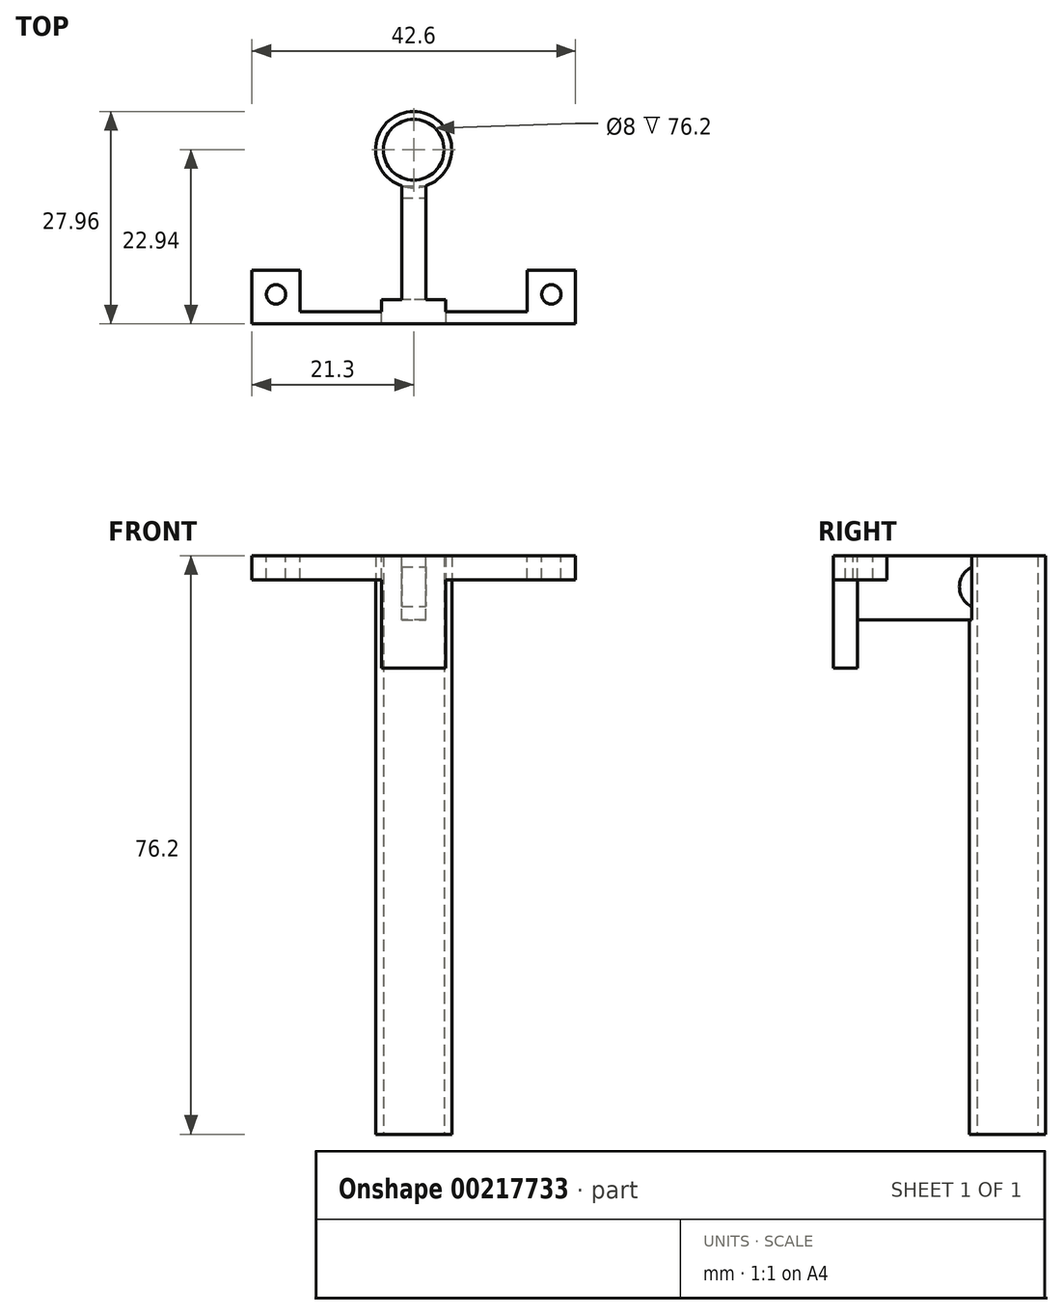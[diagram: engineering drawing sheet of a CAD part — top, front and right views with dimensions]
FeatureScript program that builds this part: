
annotation { "Feature Type Name" : "Feature", "Feature Type Description" : "" }
export const myFeature = defineFeature(function(context is Context, id is Id, definition is map)
    precondition{}
    {
        {
            var Q0;
            Q0=qCreatedBy(makeId("Top.planeOp"),FACE);
            var sketch = newSketch(context, id + "F0", { "sketchPlane" : qUnion([Q0])});
            skCircle(sketch, "E0", {"center": v(0, 0) * mm, "radius": 4 * mm});
            skCircle(sketch, "E1", {"center": v(0, 0) * mm, "radius": 5.02 * mm});
            skSolve(sketch);
        }
        {
            var Q0;
            Q0 = qSketchRegion(id + "F0", true);
            extrude(context, id + "F1", {"entities" : qUnion([Q0]), "depth" : 76.2 * mm});
        }
        {
            var Q0;
            Q0=makeQuery(id+"F1.opExtrude","CAP_FACE",FACE,{"disambiguationData":[OSD([sQuery(id+"F0.wireOp",EDGE,"E0"),sQuery(id+"F0.wireOp",EDGE,"E1")])],"isStart":false});
            var sketch = newSketch(context, id + "F2", { "sketchPlane" : qUnion([Q0])});
            skLineSegment(sketch, "E2", {"start": v(0, 0) * mm, "end": v(0, -4.76) * mm});
            skLineSegment(sketch, "E3", {"start": v(0, -22.94) * mm, "end": v(-4.24, -22.94) * mm});
            skLineSegment(sketch, "E4", {"start": v(0, -22.94) * mm, "end": v(4.24, -22.94) * mm});
            skLineSegment(sketch, "E5", {"start": v(4.24, -22.94) * mm, "end": v(4.24, -19.77) * mm});
            skLineSegment(sketch, "E6", {"start": v(4.24, -19.77) * mm, "end": v(1.59, -19.77) * mm});
            skLineSegment(sketch, "E7", {"start": v(-4.24, -19.77) * mm, "end": v(-4.24, -22.94) * mm});
            skLineSegment(sketch, "E8", {"start": v(1.59, -5.02) * mm, "end": v(1.59, -19.77) * mm});
            skLineSegment(sketch, "E9", {"start": v(-1.59, -19.77) * mm, "end": v(-1.59, -4.76) * mm});
            skLineSegment(sketch, "E10", {"start": v(1.59, -5.02) * mm, "end": v(1.59, -4.76) * mm});
            skLineSegment(sketch, "E11", {"start": v(1.59, -4.76) * mm, "end": v(-1.59, -4.76) * mm});
            skLineSegment(sketch, "E12.trimOffspring", {"start": v(-1.59, -19.77) * mm, "end": v(-4.24, -19.77) * mm});
            skSolve(sketch);
        }
        {
            var Q0;
            Q0 = qSketchRegion(id + "F2", true);
            extrude(context, id + "F3", {"entities" : qUnion([Q0]), "operationType" : NewBodyOperationType.ADD, "oppositeDirection" : true, "depth" : 8.48 * mm});
        }
        {
            var Q0;
            Q0=makeQuery(id+"F3.opExtrude","SWEPT_FACE",FACE,{"disambiguationData":[OSD([sQuery(id+"F2.wireOp",EDGE,"E8"),sQuery(id+"F2.wireOp",EDGE,"E10")])]});
            var sketch = newSketch(context, id + "F4", { "sketchPlane" : qUnion([Q0])});
            skArc(sketch, "E13", {"start": v(-4.76, 74.68) * mm, "mid": v(-6.35, 72.08) * mm, "end": v(-4.76, 69.48) * mm});
            skLineSegment(sketch, "E14", {"start": v(-4.76, 69.48) * mm, "end": v(-4.76, 74.68) * mm});
            skSolve(sketch);
        }
        {
            var Q0;
            Q0 = qSketchRegion(id + "F4", true);
            extrude(context, id + "F5", {"entities" : qUnion([Q0]), "operationType" : NewBodyOperationType.REMOVE, "oppositeDirection" : true, "depth" : 25.4 * mm});
        }
        {
            var Q0;
            Q0=makeQuery(id+"F3.boolean.opBoolean","MERGE",FACE,{"derivedFrom":[makeQuery(id+"F1.opExtrude","CAP_FACE",FACE,{"disambiguationData":[OSD([sQuery(id+"F0.wireOp",EDGE,"E0"),sQuery(id+"F0.wireOp",EDGE,"E1")])],"isStart":false}),makeQuery(id+"F3.opExtrude","CAP_FACE",FACE,{"disambiguationData":[OSD([sQuery(id+"F2.wireOp",EDGE,"E3"),sQuery(id+"F2.wireOp",EDGE,"E4"),sQuery(id+"F2.wireOp",EDGE,"E5"),sQuery(id+"F2.wireOp",EDGE,"E6"),sQuery(id+"F2.wireOp",EDGE,"E7"),sQuery(id+"F2.wireOp",EDGE,"E8"),sQuery(id+"F2.wireOp",EDGE,"E9"),sQuery(id+"F2.wireOp",EDGE,"E10"),sQuery(id+"F2.wireOp",EDGE,"E11"),sQuery(id+"F2.wireOp",EDGE,"E12.trimOffspring")])],"isStart":true})]});
            var sketch = newSketch(context, id + "F6", { "sketchPlane" : qUnion([Q0])});
            skLineSegment(sketch, "E15", {"start": v(0, -22.94) * mm, "end": v(-18.13, -22.94) * mm});
            skLineSegment(sketch, "E16", {"start": v(-18.13, -20.32) * mm, "end": v(-18.13, -19.05) * mm});
            skCircle(sketch, "E17", {"center": v(-18.13, -19.05) * mm, "radius": 1.27 * mm});
            skLineSegment(sketch, "E18.bottom", {"start": v(-14.95, -15.87) * mm, "end": v(-21.3, -15.87) * mm});
            skLineSegment(sketch, "E18.left", {"start": v(-14.95, -15.87) * mm, "end": v(-14.95, -21.36) * mm});
            skLineSegment(sketch, "E18.right", {"start": v(-21.3, -15.87) * mm, "end": v(-21.3, -22.22) * mm});
            skLineSegment(sketch, "E19", {"start": v(-4.24, -22.94) * mm, "end": v(-21.3, -22.94) * mm});
            skLineSegment(sketch, "E20", {"start": v(-21.3, -22.94) * mm, "end": v(-21.3, -22.22) * mm});
            skLineSegment(sketch, "E21", {"start": v(-4.24, -21.36) * mm, "end": v(-14.95, -21.36) * mm});
            skPoint(sketch, "E22.start.orphan", {"position": v(-14.95, -22.22) * mm});
            skLineSegment(sketch, "E23.MirrorCS", {"start": v(0, -22.94) * mm, "end": v(18.13, -22.94) * mm});
            skLineSegment(sketch, "E24.MirrorCS", {"start": v(21.3, -22.94) * mm, "end": v(21.3, -22.22) * mm});
            skLineSegment(sketch, "E25.MirrorCS", {"start": v(18.13, -20.32) * mm, "end": v(18.13, -19.05) * mm});
            skPoint(sketch, "E26.MirrorP", {"position": v(14.95, -22.22) * mm});
            skPoint(sketch, "E27.MirrorP", {"position": v(18.13, -19.05) * mm});
            skCircle(sketch, "E28.MirrorC", {"center": v(18.13, -19.05) * mm, "radius": 1.27 * mm});
            skLineSegment(sketch, "E29.MirrorCS", {"start": v(14.95, -15.87) * mm, "end": v(21.3, -15.87) * mm});
            skLineSegment(sketch, "E30.MirrorCS", {"start": v(4.24, -21.36) * mm, "end": v(14.95, -21.36) * mm});
            skLineSegment(sketch, "E31.MirrorCS", {"start": v(4.24, -22.94) * mm, "end": v(21.3, -22.94) * mm});
            skLineSegment(sketch, "E32.MirrorCS", {"start": v(21.3, -15.87) * mm, "end": v(21.3, -22.22) * mm});
            skLineSegment(sketch, "E33.MirrorCS", {"start": v(14.95, -15.87) * mm, "end": v(14.95, -21.36) * mm});
            skLineSegment(sketch, "E34", {"start": v(4.24, -21.36) * mm, "end": v(-4.24, -21.36) * mm});
            skSolve(sketch);
        }
        {
            var Q0;
            {var subQ1=sQuery(id+"F6.wireOp",EDGE,"E24.MirrorCS");Q0=makeQuery(id+"F6.imprint","IMPRINT",FACE,{"disambiguationData":[TD([[makeQuery(id+"F6.imprint","IMPRINT",EDGE,{"derivedFrom":subQ1}),1.0]])]});}
            var Q1;
            {var subQ3=sQuery(id+"F6.wireOp",EDGE,"E15");Q1=makeQuery(id+"F6.imprint","IMPRINT",FACE,{"disambiguationData":[TD([[makeQuery(id+"F6.imprint","IMPRINT",EDGE,{"derivedFrom":subQ3}),-1.0]])]});}
            var Q2;
            Q2=makeQuery(id+"F6.imprint","IMPRINT",FACE,{"disambiguationData":[TD([[makeQuery(id+"F6.imprint","IMPRINT",EDGE,{"derivedFrom":sQuery(id+"F6.wireOp",EDGE,"E17")}),-1.0]])]});
            extrude(context, id + "F7", {"entities" : qUnion([Q0, Q1, Q2]), "operationType" : NewBodyOperationType.ADD, "oppositeDirection" : true, "depth" : 3.17 * mm});
        }
        {
            var Q0;
            Q0=makeQuery(id+"F3.opExtrude","CAP_FACE",FACE,{"disambiguationData":[OSD([sQuery(id+"F2.wireOp",EDGE,"E3"),sQuery(id+"F2.wireOp",EDGE,"E4"),sQuery(id+"F2.wireOp",EDGE,"E5"),sQuery(id+"F2.wireOp",EDGE,"E6"),sQuery(id+"F2.wireOp",EDGE,"E7"),sQuery(id+"F2.wireOp",EDGE,"E8"),sQuery(id+"F2.wireOp",EDGE,"E9"),sQuery(id+"F2.wireOp",EDGE,"E10"),sQuery(id+"F2.wireOp",EDGE,"E11"),sQuery(id+"F2.wireOp",EDGE,"E12.trimOffspring")])],"isStart":false});
            var sketch = newSketch(context, id + "F8", { "sketchPlane" : qUnion([Q0])});
            skLineSegment(sketch, "E35.bottom", {"start": v(4.24, 19.77) * mm, "end": v(-4.24, 19.77) * mm});
            skLineSegment(sketch, "E35.top", {"start": v(4.24, 22.94) * mm, "end": v(-4.24, 22.94) * mm});
            skLineSegment(sketch, "E35.left", {"start": v(4.24, 19.77) * mm, "end": v(4.24, 22.94) * mm});
            skLineSegment(sketch, "E35.right", {"start": v(-4.24, 19.77) * mm, "end": v(-4.24, 22.94) * mm});
            skSolve(sketch);
        }
        {
            var Q0;
            Q0 = qSketchRegion(id + "F8", true);
            extrude(context, id + "F9", {"entities" : qUnion([Q0]), "operationType" : NewBodyOperationType.ADD, "depth" : 6.35 * mm});
        }
    });
